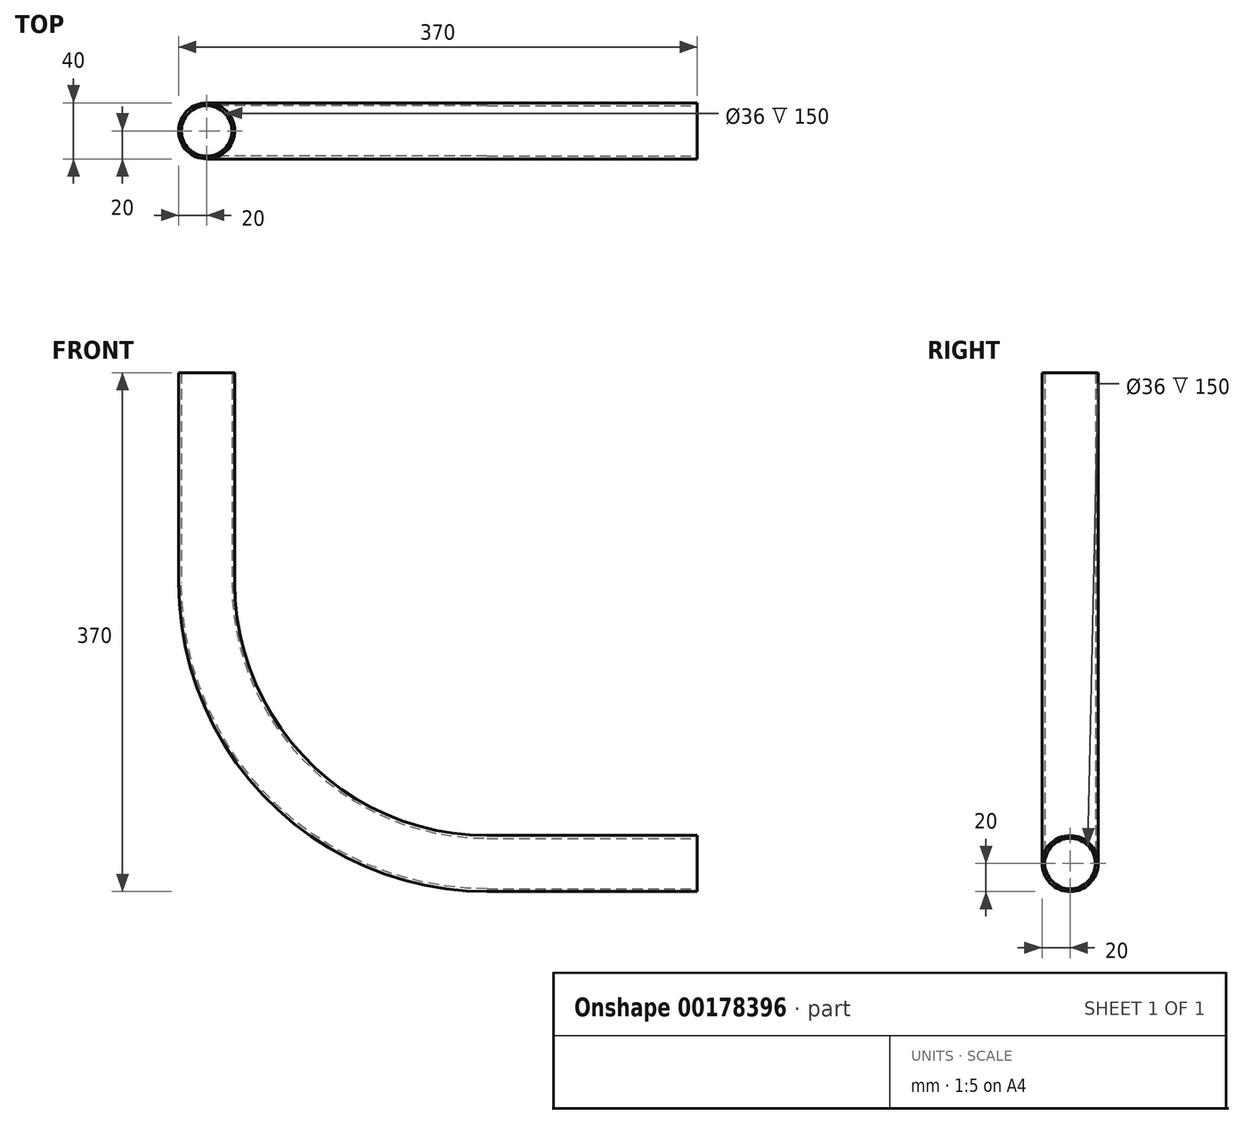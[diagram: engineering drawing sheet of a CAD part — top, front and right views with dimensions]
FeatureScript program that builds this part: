
annotation { "Feature Type Name" : "Feature", "Feature Type Description" : "" }
export const myFeature = defineFeature(function(context is Context, id is Id, definition is map)
    precondition{}
    {
        {
            var Q0;
            Q0=qCreatedBy(makeId("Front.planeOp"),FACE);
            var sketch = newSketch(context, id + "F0", { "sketchPlane" : qUnion([Q0])});
            skLineSegment(sketch, "E0", {"start": v(0, 200) * mm, "end": v(0, 350) * mm});
            skLineSegment(sketch, "E1", {"start": v(200, 0) * mm, "end": v(350, 0) * mm});
            skPoint(sketch, "E2.visualSharp", {"position": v(0, 0) * mm});
            skArc(sketch, "E2.filletArc", {"start": v(0, 200) * mm, "mid": v(58.58, 58.58) * mm, "end": v(200, 0) * mm});
            skSolve(sketch);
        }
        {
            var Q0;
            Q0=sQuery(id+"F0.wireOp",VERTEX,"E0.end");
            var Q1;
            Q1=qCreatedBy(makeId("Top.planeOp"),FACE);
            cPlane(context, id + "F1", {"entities" : qUnion([Q0, Q1]), "cplaneType" : CPlaneType.PLANE_POINT, "offset" : 25 * mm, "width" : 150 * mm, "height" : 150 * mm});
        }
        {
            var Q0;
            Q0=qCreatedBy(id+"F1.planeOp",FACE);
            var sketch = newSketch(context, id + "F2", { "sketchPlane" : qUnion([Q0])});
            skCircle(sketch, "E3", {"center": v(0, 0) * mm, "radius": 20 * mm});
            skCircle(sketch, "E4.0", {"center": v(0, 0) * mm, "radius": 18 * mm});
            skSolve(sketch);
        }
        {
            var Q0;
            Q0=makeQuery(id+"F2.imprint","IMPRINT",FACE,{"disambiguationData":[TD([[makeQuery(id+"F2.imprint","IMPRINT",EDGE,{"derivedFrom":sQuery(id+"F2.wireOp",EDGE,"E3")}),1.0]])]});
            var Q1;
            Q1=sQuery(id+"F0.wireOp",EDGE,"E0");
            var Q2;
            Q2=sQuery(id+"F0.wireOp",EDGE,"E2.filletArc");
            var Q3;
            Q3=sQuery(id+"F0.wireOp",EDGE,"E1");
            sweep(context, id + "F3", {"profiles" : qUnion([Q0]), "path" : qUnion([Q1, Q2, Q3])});
        }
    });
